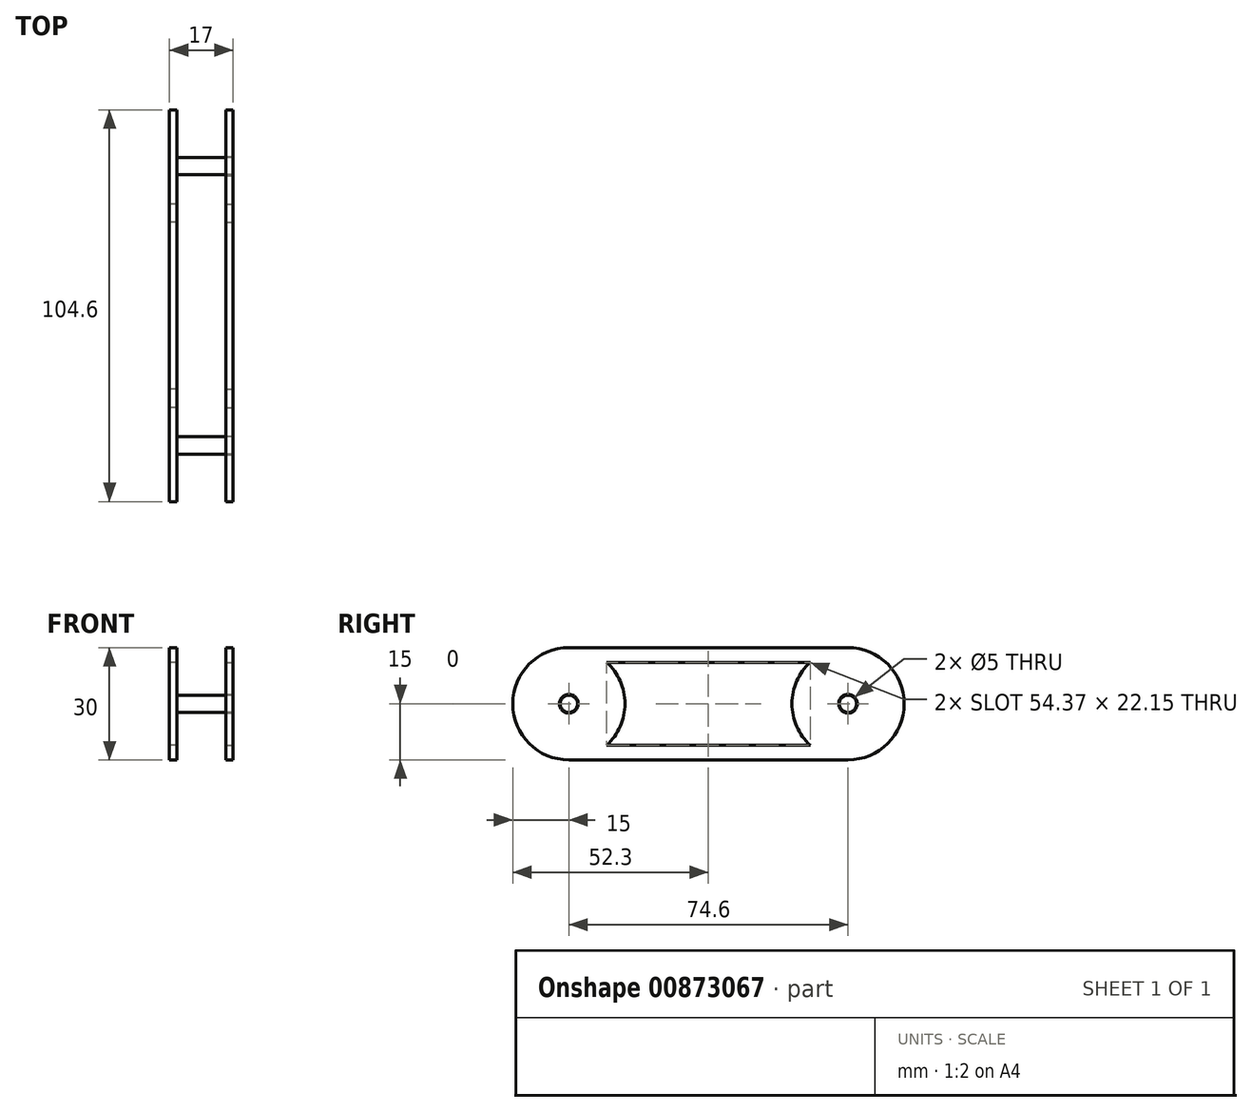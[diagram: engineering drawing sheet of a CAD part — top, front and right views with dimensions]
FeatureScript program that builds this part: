
annotation { "Feature Type Name" : "Feature", "Feature Type Description" : "" }
export const myFeature = defineFeature(function(context is Context, id is Id, definition is map)
    precondition{}
    {
        {
            var Q0;
            Q0=qCreatedBy(makeId("Right.planeOp"),FACE);
            var sketch = newSketch(context, id + "F0", { "sketchPlane" : qUnion([Q0])});
            skCircle(sketch, "E0", {"center": v(0, 0) * mm, "radius": 2.3 * mm});
            skCircle(sketch, "E1", {"center": v(0, 0) * mm, "radius": 15 * mm});
            skCircle(sketch, "E2", {"center": v(74.6, 0) * mm, "radius": 2.3 * mm});
            skCircle(sketch, "E3", {"center": v(74.6, 0) * mm, "radius": 15 * mm});
            skCircle(sketch, "E4", {"center": v(0, 0) * mm, "radius": 12.5 * mm});
            skCircle(sketch, "E5", {"center": v(74.6, 0) * mm, "radius": 12.5 * mm});
            skLineSegment(sketch, "E6", {"start": v(0, 15) * mm, "end": v(74.6, 15) * mm});
            skLineSegment(sketch, "E7", {"start": v(0, -15) * mm, "end": v(74.6, -15) * mm});
            skLineSegment(sketch, "E8", {"start": v(10.12, 11.08) * mm, "end": v(64.48, 11.08) * mm});
            skLineSegment(sketch, "E9", {"start": v(64.48, 11.08) * mm, "end": v(64.48, -11.08) * mm});
            skLineSegment(sketch, "E10", {"start": v(64.48, -11.08) * mm, "end": v(10.12, -11.08) * mm});
            skLineSegment(sketch, "E11", {"start": v(10.12, -11.08) * mm, "end": v(10.12, 11.08) * mm});
            skSolve(sketch);
        }
        {
            var Q0;
            {var subQ0=sQuery(id+"F0.wireOp",EDGE,"E11");var subQ4=sQuery(id+"F0.wireOp",EDGE,"E4");var subQ5=makeQuery(id+"F0.imprint","INTERSECT",VERTEX,{"disambiguationData":[OD(0.0)],"derivedFrom":[subQ4,subQ0]});Q0=makeQuery(id+"F0.imprint","IMPRINT",FACE,{"disambiguationData":[TD([[makeQuery(id+"F0.imprint","IMPRINT",EDGE,{"disambiguationData":[TD([[subQ5,-1.0]])],"derivedFrom":subQ4}),-1.0]])]});}
            var Q1;
            {var subQ0=sQuery(id+"F0.wireOp",EDGE,"E11");var subQ1=sQuery(id+"F0.wireOp",EDGE,"E4");var subQ2=makeQuery(id+"F0.imprint","INTERSECT",VERTEX,{"disambiguationData":[OD(0.0)],"derivedFrom":[subQ1,subQ0]});Q1=makeQuery(id+"F0.imprint","IMPRINT",FACE,{"disambiguationData":[TD([[makeQuery(id+"F0.imprint","IMPRINT",EDGE,{"disambiguationData":[TD([[subQ2,-1.0]])],"derivedFrom":subQ1}),1.0]])]});}
            var Q2;
            Q2=makeQuery(id+"F0.imprint","IMPRINT",FACE,{"disambiguationData":[TD([[makeQuery(id+"F0.imprint","IMPRINT",EDGE,{"derivedFrom":sQuery(id+"F0.wireOp",EDGE,"E0")}),-1.0]])]});
            var Q3;
            {var subQ4=sQuery(id+"F0.wireOp",EDGE,"E1");var subQ7=makeQuery(id+"F0.imprint","INTERSECT",VERTEX,{"derivedFrom":[subQ4,sQuery(id+"F0.wireOp",EDGE,"E6")]});Q3=makeQuery(id+"F0.imprint","IMPRINT",FACE,{"disambiguationData":[TD([[makeQuery(id+"F0.imprint","IMPRINT",EDGE,{"disambiguationData":[TD([[subQ7,-1.0]])],"derivedFrom":subQ4}),1.0]])]});}
            var Q4;
            {var subQ0=sQuery(id+"F0.wireOp",EDGE,"E6");Q4=makeQuery(id+"F0.imprint","IMPRINT",FACE,{"disambiguationData":[TD([[makeQuery(id+"F0.imprint","IMPRINT",EDGE,{"derivedFrom":subQ0}),-1.0]])]});}
            var Q5;
            {var subQ0=sQuery(id+"F0.wireOp",EDGE,"E7");Q5=makeQuery(id+"F0.imprint","IMPRINT",FACE,{"disambiguationData":[TD([[makeQuery(id+"F0.imprint","IMPRINT",EDGE,{"derivedFrom":subQ0}),1.0]])]});}
            var Q6;
            {var subQ0=sQuery(id+"F0.wireOp",EDGE,"E3");var subQ1=makeQuery(id+"F0.imprint","INTERSECT",VERTEX,{"derivedFrom":[subQ0,sQuery(id+"F0.wireOp",EDGE,"E6")]});Q6=makeQuery(id+"F0.imprint","IMPRINT",FACE,{"disambiguationData":[TD([[makeQuery(id+"F0.imprint","IMPRINT",EDGE,{"disambiguationData":[TD([[subQ1,1.0]])],"derivedFrom":subQ0}),1.0]])]});}
            var Q7;
            Q7=makeQuery(id+"F0.imprint","IMPRINT",FACE,{"disambiguationData":[TD([[makeQuery(id+"F0.imprint","IMPRINT",EDGE,{"derivedFrom":sQuery(id+"F0.wireOp",EDGE,"E2")}),-1.0]])]});
            var Q8;
            {var subQ0=sQuery(id+"F0.wireOp",EDGE,"E9");var subQ1=sQuery(id+"F0.wireOp",EDGE,"E5");var subQ2=makeQuery(id+"F0.imprint","INTERSECT",VERTEX,{"disambiguationData":[OD(0.0)],"derivedFrom":[subQ1,subQ0]});Q8=makeQuery(id+"F0.imprint","IMPRINT",FACE,{"disambiguationData":[TD([[makeQuery(id+"F0.imprint","IMPRINT",EDGE,{"disambiguationData":[TD([[subQ2,-1.0]])],"derivedFrom":subQ1}),1.0]])]});}
            var Q9;
            {var subQ0=sQuery(id+"F0.wireOp",EDGE,"E9");var subQ4=sQuery(id+"F0.wireOp",EDGE,"E5");var subQ5=makeQuery(id+"F0.imprint","INTERSECT",VERTEX,{"disambiguationData":[OD(0.0)],"derivedFrom":[subQ4,subQ0]});Q9=makeQuery(id+"F0.imprint","IMPRINT",FACE,{"disambiguationData":[TD([[makeQuery(id+"F0.imprint","IMPRINT",EDGE,{"disambiguationData":[TD([[subQ5,-1.0]])],"derivedFrom":subQ4}),-1.0]])]});}
            extrude(context, id + "F1", {"entities" : qUnion([Q0, Q1, Q2, Q3, Q4, Q5, Q6, Q7, Q8, Q9]), "depth" : 2 * mm, "offsetDistance" : 25 * mm});
        }
        {
            var Q0;
            Q0=makeQuery(id+"F0.imprint","IMPRINT",FACE,{"disambiguationData":[TD([[makeQuery(id+"F0.imprint","IMPRINT",EDGE,{"derivedFrom":sQuery(id+"F0.wireOp",EDGE,"E0")}),1.0]])]});
            var Q1;
            Q1=makeQuery(id+"F0.imprint","IMPRINT",FACE,{"disambiguationData":[TD([[makeQuery(id+"F0.imprint","IMPRINT",EDGE,{"derivedFrom":sQuery(id+"F0.wireOp",EDGE,"E2")}),1.0]])]});
            extrude(context, id + "F2", {"entities" : qUnion([Q0, Q1]), "operationType" : NewBodyOperationType.ADD, "depth" : 17 * mm, "offsetDistance" : 25 * mm});
        }
        {
            var Q0;
            Q0=makeQuery(id+"F2.opExtrude","CAP_FACE",FACE,{"disambiguationData":[OSD([sQuery(id+"F0.wireOp",EDGE,"E0")])],"isStart":false});
            var sketch = newSketch(context, id + "F3", { "sketchPlane" : qUnion([Q0])});
            skLineSegment(sketch, "E12.0.0", {"start": v(74.6, 15) * mm, "end": v(0, 15) * mm});
            skArc(sketch, "E12.0.1", {"start": v(0, 15) * mm, "mid": v(-15, 0) * mm, "end": v(0, -15) * mm});
            skLineSegment(sketch, "E12.0.2", {"start": v(0, -15) * mm, "end": v(74.6, -15) * mm});
            skArc(sketch, "E12.0.3", {"start": v(74.6, -15) * mm, "mid": v(89.6, 0) * mm, "end": v(74.6, 15) * mm});
            skArc(sketch, "E13.0", {"start": v(10.12, -11.08) * mm, "mid": v(15, 0) * mm, "end": v(10.12, 11.08) * mm});
            skArc(sketch, "E14.0", {"start": v(64.48, 11.08) * mm, "mid": v(59.6, 0) * mm, "end": v(64.48, -11.08) * mm});
            skLineSegment(sketch, "E15.0", {"start": v(10.12, 11.08) * mm, "end": v(64.48, 11.08) * mm});
            skLineSegment(sketch, "E16.0", {"start": v(64.48, -11.08) * mm, "end": v(10.12, -11.08) * mm});
            skCircle(sketch, "E17.0", {"center": v(74.6, 0) * mm, "radius": 2.3 * mm});
            skCircle(sketch, "E18.0", {"center": v(0, 0) * mm, "radius": 2.3 * mm});
            skCircle(sketch, "E19", {"center": v(0, 0) * mm, "radius": 2.5 * mm});
            skCircle(sketch, "E20", {"center": v(74.6, 0) * mm, "radius": 2.5 * mm});
            skSolve(sketch);
        }
        {
            var Q0;
            Q0=makeQuery(id+"F3.imprint","IMPRINT",FACE,{"disambiguationData":[TD([[makeQuery(id+"F3.imprint","IMPRINT",EDGE,{"derivedFrom":sQuery(id+"F3.wireOp",EDGE,"E12.0.0")}),1.0]])]});
            extrude(context, id + "F4", {"entities" : qUnion([Q0]), "oppositeDirection" : true, "depth" : 2 * mm, "offsetDistance" : 25 * mm});
        }
    });
